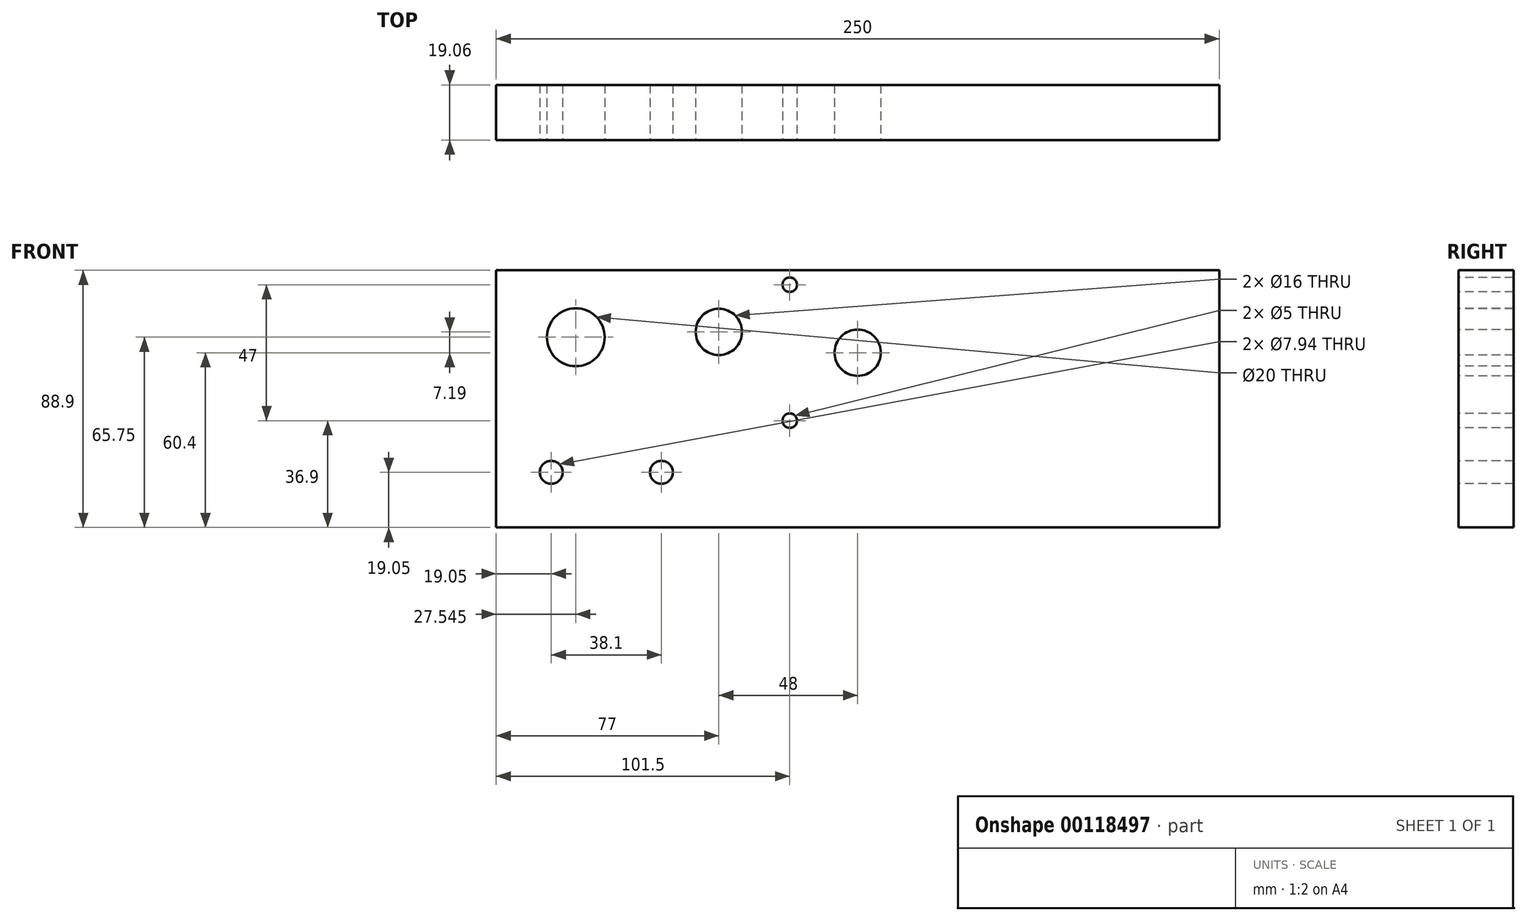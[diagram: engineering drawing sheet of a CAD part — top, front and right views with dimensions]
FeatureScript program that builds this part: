
annotation { "Feature Type Name" : "Feature", "Feature Type Description" : "" }
export const myFeature = defineFeature(function(context is Context, id is Id, definition is map)
    precondition{}
    {
        {
            var Q0;
            Q0=qCreatedBy(makeId("Front.planeOp"),FACE);
            var sketch = newSketch(context, id + "F0", { "sketchPlane" : qUnion([Q0])});
            skLineSegment(sketch, "E0.bottom", {"start": v(125, 44.45) * mm, "end": v(-125, 44.45) * mm});
            skLineSegment(sketch, "E0.top", {"start": v(125, -44.45) * mm, "end": v(-125, -44.45) * mm});
            skLineSegment(sketch, "E0.left", {"start": v(125, 44.45) * mm, "end": v(125, -44.45) * mm});
            skLineSegment(sketch, "E0.right", {"start": v(-125, 44.45) * mm, "end": v(-125, -44.45) * mm});
            skPoint(sketch, "E0.middle", {"position": v(0, 0) * mm});
            skSolve(sketch);
        }
        {
            var Q0;
            Q0 = qSketchRegion(id + "F0", true);
            extrude(context, id + "F1", {"entities" : qUnion([Q0]), "depth" : 19.05 * mm, "symmetric" : true});
        }
        {
            var Q0;
            Q0=makeQuery(id+"F1.opExtrude","CAP_FACE",FACE,{"disambiguationData":[OSD([sQuery(id+"F0.wireOp",EDGE,"E0.bottom"),sQuery(id+"F0.wireOp",EDGE,"E0.top"),sQuery(id+"F0.wireOp",EDGE,"E0.left"),sQuery(id+"F0.wireOp",EDGE,"E0.right")])],"isStart":false});
            var sketch = newSketch(context, id + "F2", { "sketchPlane" : qUnion([Q0])});
            skCircle(sketch, "E1", {"center": v(-105.95, -25.4) * mm, "radius": 3.97 * mm});
            skCircle(sketch, "E2", {"center": v(-67.85, -25.4) * mm, "radius": 3.97 * mm});
            skCircle(sketch, "E3", {"center": v(-97.45, 21.3) * mm, "radius": 10 * mm});
            skCircle(sketch, "E4", {"center": v(-48, 23.14) * mm, "radius": 8 * mm});
            skCircle(sketch, "E5", {"center": v(-23.5, 39.45) * mm, "radius": 2.5 * mm});
            skCircle(sketch, "E6", {"center": v(-23.5, -7.55) * mm, "radius": 2.5 * mm});
            skCircle(sketch, "E7", {"center": v(0, 15.95) * mm, "radius": 8 * mm});
            skLineSegment(sketch, "E8", {"start": v(0, 44.45) * mm, "end": v(0, -44.45) * mm, "construction": true});
            skLineSegment(sketch, "E9", {"start": v(-125, -25.4) * mm, "end": v(0, -25.4) * mm, "construction": true});
            skLineSegment(sketch, "E10.bottom", {"start": v(23.5, 39.45) * mm, "end": v(-23.5, 39.45) * mm, "construction": true});
            skLineSegment(sketch, "E10.top", {"start": v(23.5, -7.55) * mm, "end": v(-23.5, -7.55) * mm, "construction": true});
            skLineSegment(sketch, "E10.left", {"start": v(23.5, 39.45) * mm, "end": v(23.5, -7.55) * mm, "construction": true});
            skLineSegment(sketch, "E10.right", {"start": v(-23.5, 39.45) * mm, "end": v(-23.5, -7.55) * mm, "construction": true});
            skSolve(sketch);
        }
        {
            var Q0;
            Q0=makeQuery(id+"F2.imprint","IMPRINT",FACE,{"disambiguationData":[TD([[makeQuery(id+"F2.imprint","IMPRINT",EDGE,{"derivedFrom":sQuery(id+"F2.wireOp",EDGE,"E4")}),1.0]])]});
            var Q1;
            Q1=makeQuery(id+"F2.imprint","IMPRINT",FACE,{"disambiguationData":[TD([[makeQuery(id+"F2.imprint","IMPRINT",EDGE,{"derivedFrom":sQuery(id+"F2.wireOp",EDGE,"E7")}),1.0]])]});
            var Q2;
            Q2=makeQuery(id+"F2.imprint","IMPRINT",FACE,{"disambiguationData":[TD([[makeQuery(id+"F2.imprint","IMPRINT",EDGE,{"derivedFrom":sQuery(id+"F2.wireOp",EDGE,"E6")}),1.0]])]});
            var Q3;
            Q3=makeQuery(id+"F2.imprint","IMPRINT",FACE,{"disambiguationData":[TD([[makeQuery(id+"F2.imprint","IMPRINT",EDGE,{"derivedFrom":sQuery(id+"F2.wireOp",EDGE,"E5")}),1.0]])]});
            var Q4;
            Q4=makeQuery(id+"F2.imprint","IMPRINT",FACE,{"disambiguationData":[TD([[makeQuery(id+"F2.imprint","IMPRINT",EDGE,{"derivedFrom":sQuery(id+"F2.wireOp",EDGE,"E3")}),1.0]])]});
            var Q5;
            Q5=makeQuery(id+"F2.imprint","IMPRINT",FACE,{"disambiguationData":[TD([[makeQuery(id+"F2.imprint","IMPRINT",EDGE,{"derivedFrom":sQuery(id+"F2.wireOp",EDGE,"E2")}),1.0]])]});
            var Q6;
            Q6=makeQuery(id+"F2.imprint","IMPRINT",FACE,{"disambiguationData":[TD([[makeQuery(id+"F2.imprint","IMPRINT",EDGE,{"derivedFrom":sQuery(id+"F2.wireOp",EDGE,"E1")}),1.0]])]});
            var Q7;
            Q7=sQuery(id+"F2.wireOp",EDGE,"E3");
            var Q8;
            Q8=sQuery(id+"F2.wireOp",EDGE,"E1");
            var Q9;
            Q9=sQuery(id+"F2.wireOp",EDGE,"E2");
            var Q10;
            Q10=sQuery(id+"F2.wireOp",EDGE,"E4");
            var Q11;
            Q11=sQuery(id+"F2.wireOp",EDGE,"E5");
            var Q12;
            Q12=sQuery(id+"F2.wireOp",EDGE,"E6");
            var Q13;
            Q13=sQuery(id+"F2.wireOp",EDGE,"E7");
            extrude(context, id + "F3", {"entities" : qUnion([Q0, Q1, Q2, Q3, Q4, Q5, Q6]), "operationType" : NewBodyOperationType.REMOVE, "surfaceEntities" : qUnion([Q7, Q8, Q9, Q10, Q11, Q12, Q13]), "oppositeDirection" : true, "depth" : 25.4 * mm});
        }
    });
